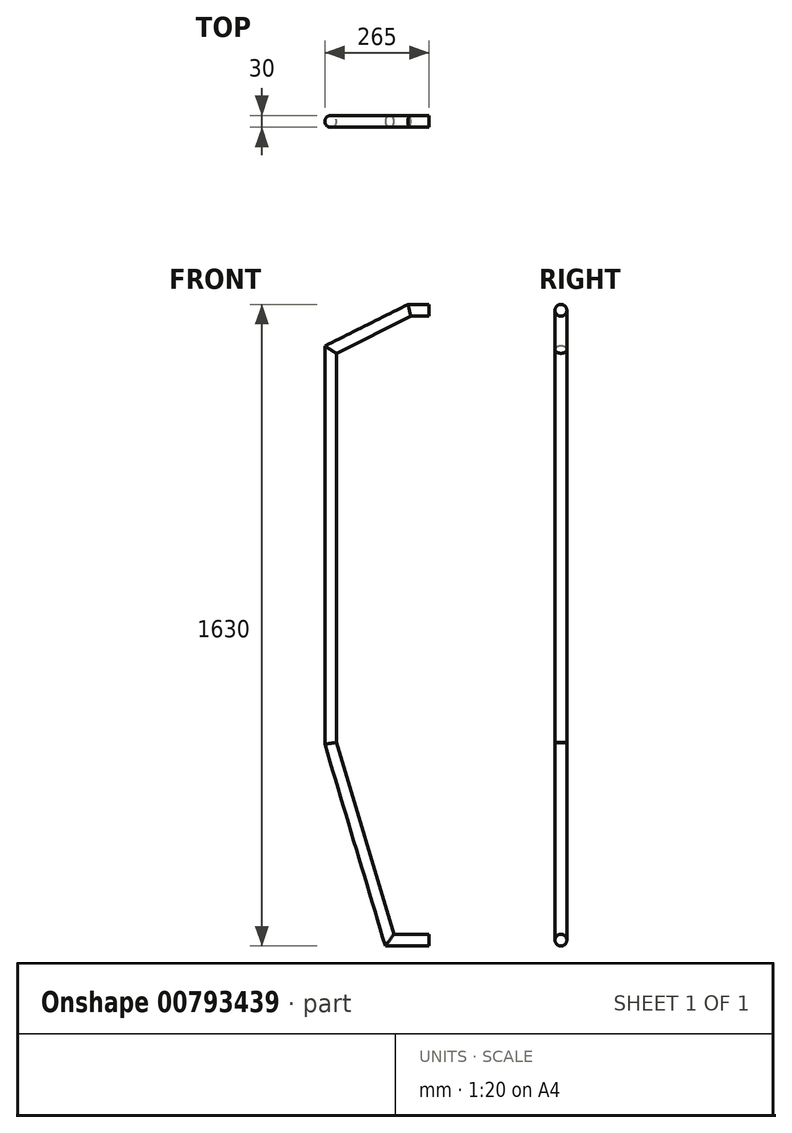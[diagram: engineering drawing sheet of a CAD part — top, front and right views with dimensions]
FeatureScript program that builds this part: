
annotation { "Feature Type Name" : "Feature", "Feature Type Description" : "" }
export const myFeature = defineFeature(function(context is Context, id is Id, definition is map)
    precondition{}
    {
        {
            var Q0;
            Q0=qCreatedBy(makeId("Front.planeOp"),FACE);
            var sketch = newSketch(context, id + "F0", { "sketchPlane" : qUnion([Q0])});
            skLineSegment(sketch, "E0", {"start": v(0, 0) * mm, "end": v(0, 1000) * mm});
            skLineSegment(sketch, "E1", {"start": v(250, -500) * mm, "end": v(150, -500) * mm});
            skLineSegment(sketch, "E2", {"start": v(0, 0) * mm, "end": v(150, -500) * mm});
            skLineSegment(sketch, "E3", {"start": v(200, 1100) * mm, "end": v(250, 1100) * mm});
            skLineSegment(sketch, "E4", {"start": v(200, 1100) * mm, "end": v(0, 1000) * mm});
            skSolve(sketch);
        }
        {
            var Q0;
            Q0=qCreatedBy(makeId("Top.planeOp"),FACE);
            var sketch = newSketch(context, id + "F1", { "sketchPlane" : qUnion([Q0])});
            skCircle(sketch, "E5", {"center": v(0, 0) * mm, "radius": 15 * mm});
            skSolve(sketch);
        }
        {
            var Q0;
            Q0=makeQuery(id+"F1.imprint","IMPRINT",FACE,{"disambiguationData":[TD([[makeQuery(id+"F1.imprint","IMPRINT",EDGE,{"derivedFrom":sQuery(id+"F1.wireOp",EDGE,"E5")}),1.0]])]});
            var Q1;
            Q1=sQuery(id+"F0.wireOp",EDGE,"E0");
            var Q2;
            Q2=sQuery(id+"F0.wireOp",EDGE,"E2");
            var Q3;
            Q3=sQuery(id+"F0.wireOp",EDGE,"E1");
            var Q4;
            Q4=sQuery(id+"F0.wireOp",EDGE,"09vBgTnh-iA2f-3oaZ-7n2A-XRS5ZERJ4ORh");
            var Q5;
            Q5=sQuery(id+"F0.wireOp",EDGE,"E4");
            var Q6;
            Q6=sQuery(id+"F0.wireOp",EDGE,"E3");
            sweep(context, id + "F2", {"profiles" : qUnion([Q0]), "path" : qUnion([Q1, Q2, Q3, Q4, Q5, Q6])});
        }
    });
